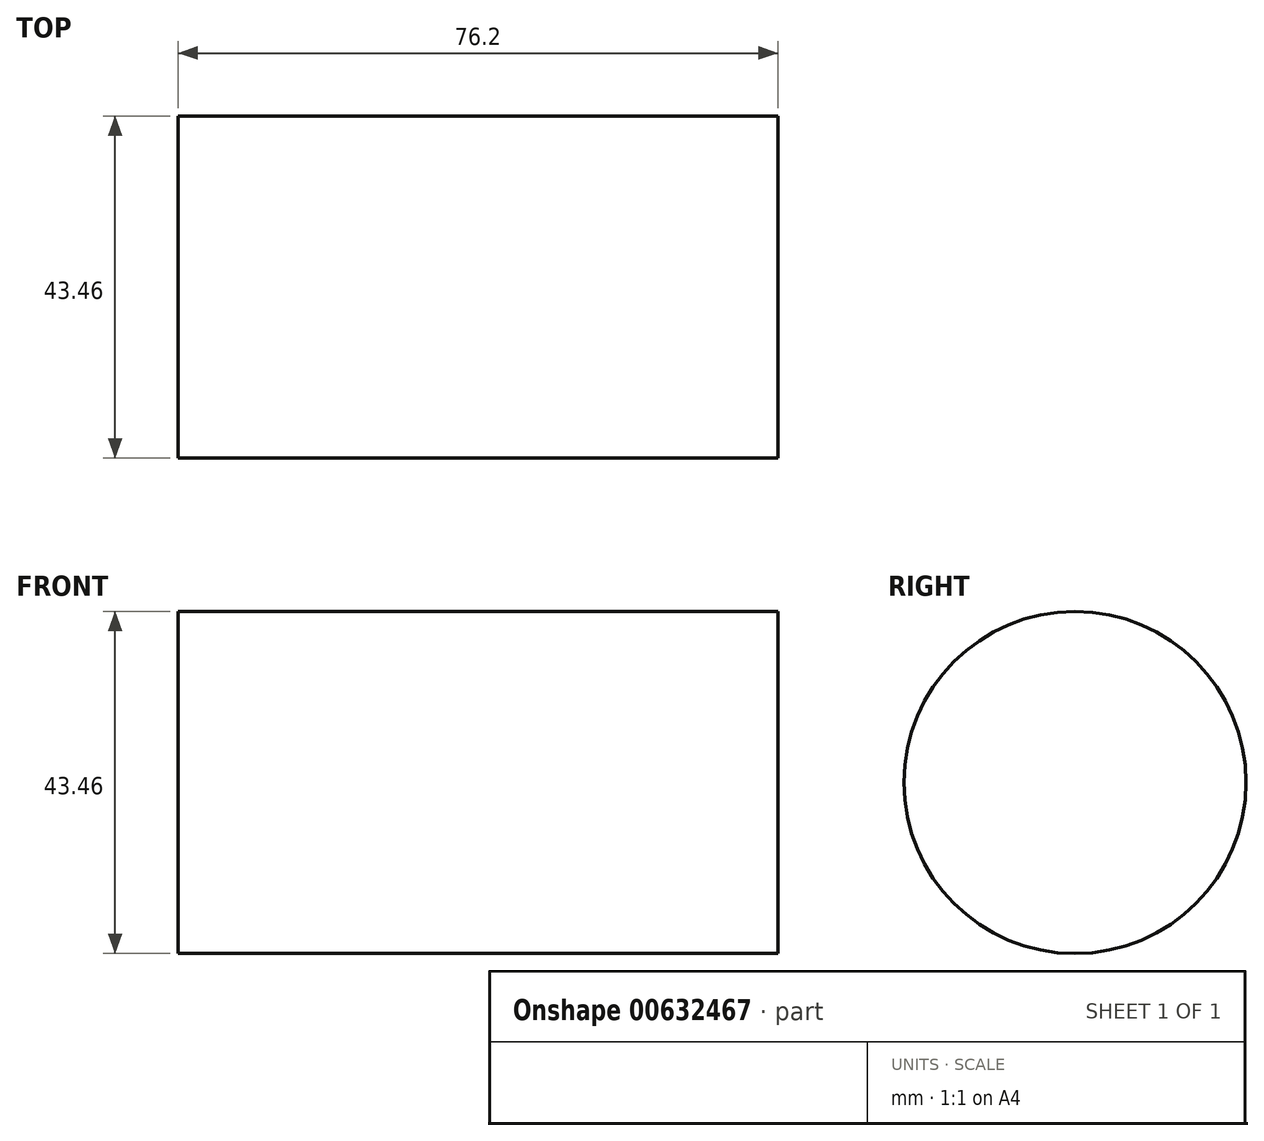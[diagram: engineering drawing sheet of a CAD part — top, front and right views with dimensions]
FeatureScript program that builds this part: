
annotation { "Feature Type Name" : "Feature", "Feature Type Description" : "" }
export const myFeature = defineFeature(function(context is Context, id is Id, definition is map)
    precondition{}
    {
        {
            var Q0;
            Q0=qCreatedBy(makeId("Right.planeOp"),FACE);
            var sketch = newSketch(context, id + "F0", { "sketchPlane" : qUnion([Q0])});
            skCircle(sketch, "E0", {"center": v(0, 0) * mm, "radius": 21.73 * mm});
            skSolve(sketch);
        }
        {
            var Q0;
            Q0 = qSketchRegion(id + "F0", true);
            extrude(context, id + "F1", {"entities" : qUnion([Q0]), "oppositeDirection" : true, "depth" : 76.2 * mm, "offsetDistance" : 25.4 * mm});
        }
    });
